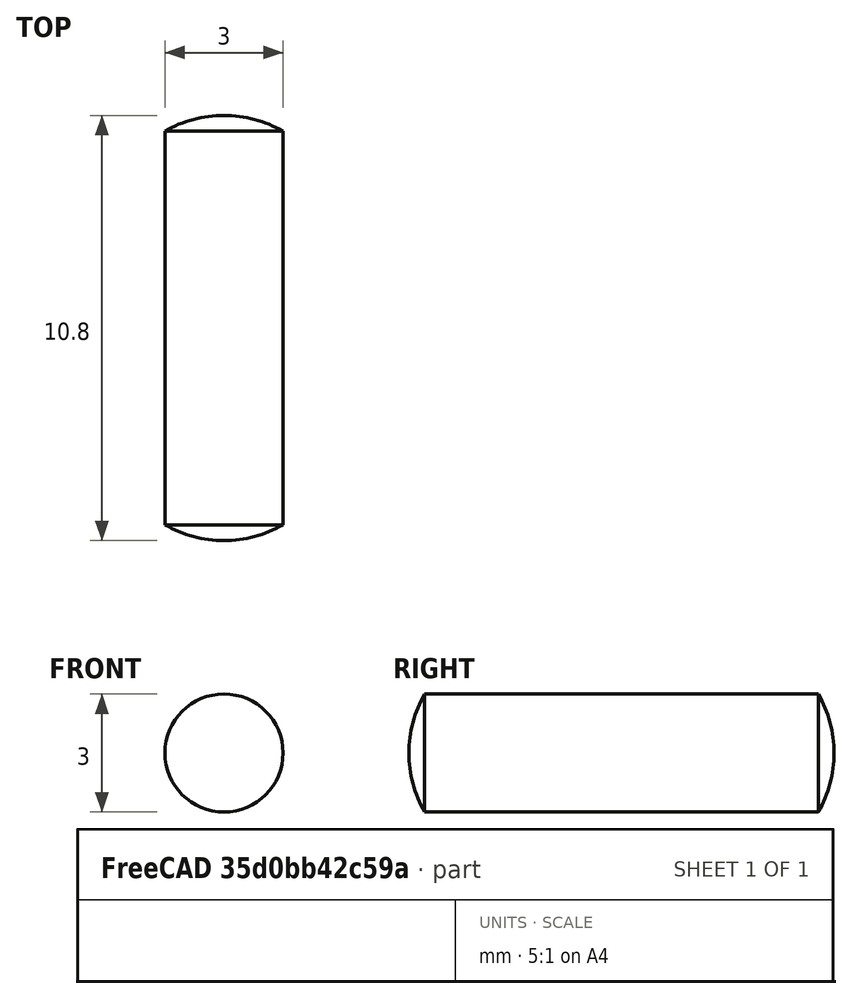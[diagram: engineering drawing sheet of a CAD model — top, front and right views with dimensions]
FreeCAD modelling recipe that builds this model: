
FCSTD DOCUMENT  (FreeCAD 0.15R4470 (Git))
Label: Zyl-Stift_DIN_7-3x10
License: CC-BY 3.0
LicenseURL: http://creativecommons.org/licenses/by/3.0/
objects: Sketcher::SketchObject×1, PartDesign::Revolution×1
note: 3 computed .brp shape members not serialized (recipe doc carries the construction recipe); baked Part::Feature solids carry a one-line shape summary decoded from their .brp

FEATURE [Sketcher::SketchObject] Sketch
  Placement = pos=(0,0,0) rot=(0.57735,0.57735,0.57735;2.0944rad)
  sketch-geometry (4):
    g0: ArcOfCircle CenterX=7.40192 CenterY=0 CenterZ=0 NormalX=0 NormalY=0 NormalZ=1 Radius=3 StartAngle=0 EndAngle=0.523599
    g1: LineSegment StartX=0 StartY=1.5 StartZ=0 EndX=10 EndY=1.5 EndZ=0
    g2: LineSegment StartX=-0.401924 StartY=0 StartZ=0 EndX=10.4019 EndY=0 EndZ=0
    g3: ArcOfCircle CenterX=2.59808 CenterY=0 CenterZ=0 NormalX=0 NormalY=0 NormalZ=1 Radius=3 StartAngle=2.61799 EndAngle=3.14159
  constraints (14):
    c: PointOnObject(g2,g-1)
    c: PointOnObject(g1,g-2)
    c: Coincident(g0,g1)
    c: PointOnObject(g0,g-1)
    c: Horizontal(g1)
    c: Coincident(g2,g0)
    c: Horizontal(g2)
    c: Radius(g0) = 3
    c: PointOnObject(g3,g2)
    c: Coincident(g3,g1)
    c: Coincident(g3,g2)
    c: Equal(g3,g0)
    c: DistanceY(g-1,g1) = 1.5
    c: DistanceX(g1) = 10
FEATURE [PartDesign::Revolution] Revolution  label="Zyl-Stift DIN 7-3x10 #"
  Angle = 360
  Axis = (0,1,0)
  Base = (0,0,0)
  Placement = pos=(0,0,0) rot=(0.57735,0.57735,0.57735;2.0944rad)
  ReferenceAxis = -> Sketch [H_Axis]
  Sketch = -> Sketch
